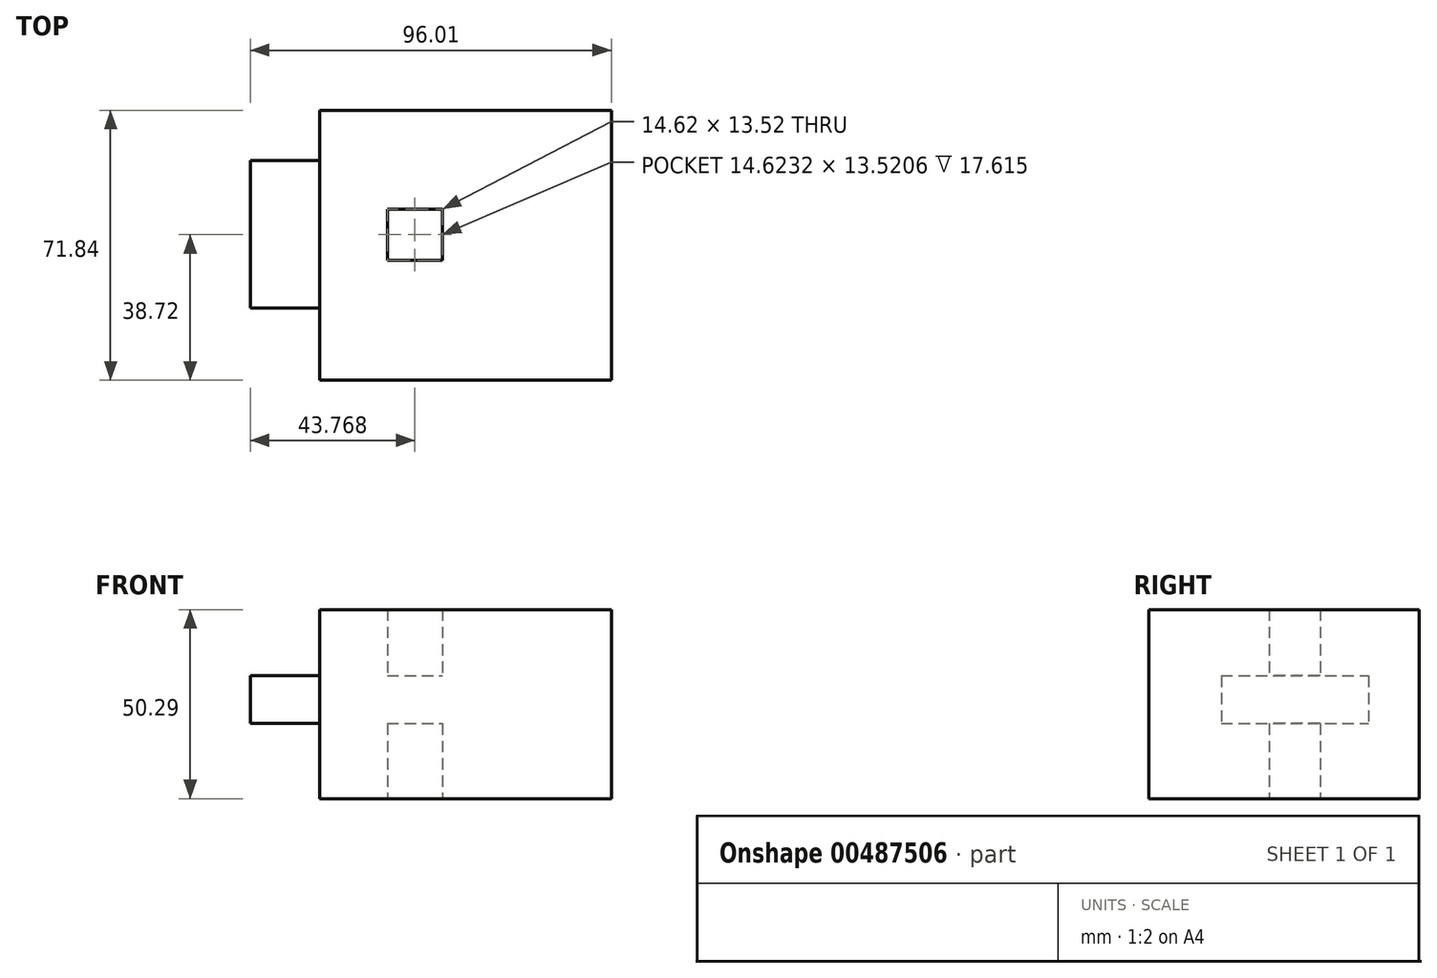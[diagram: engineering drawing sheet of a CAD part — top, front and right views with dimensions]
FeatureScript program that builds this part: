
annotation { "Feature Type Name" : "Feature", "Feature Type Description" : "" }
export const myFeature = defineFeature(function(context is Context, id is Id, definition is map)
    precondition{}
    {
        {
            var Q0;
            Q0=qCreatedBy(makeId("Top.planeOp"),FACE);
            var sketch = newSketch(context, id + "F0", { "sketchPlane" : qUnion([Q0])});
            skLineSegment(sketch, "E0.bottom", {"start": v(-32.68, 39.88) * mm, "end": v(44.93, 39.88) * mm});
            skLineSegment(sketch, "E0.top", {"start": v(-32.68, -31.96) * mm, "end": v(44.93, -31.96) * mm});
            skLineSegment(sketch, "E0.left", {"start": v(-32.68, 39.88) * mm, "end": v(-32.68, -31.96) * mm});
            skLineSegment(sketch, "E0.right", {"start": v(44.93, 39.88) * mm, "end": v(44.93, -31.96) * mm});
            skLineSegment(sketch, "E1.bottom", {"start": v(0, 0) * mm, "end": v(-14.62, 0) * mm});
            skLineSegment(sketch, "E1.top", {"start": v(0, 13.52) * mm, "end": v(-14.62, 13.52) * mm});
            skLineSegment(sketch, "E1.left", {"start": v(0, 0) * mm, "end": v(0, 13.52) * mm});
            skLineSegment(sketch, "E1.right", {"start": v(-14.62, 0) * mm, "end": v(-14.62, 13.52) * mm});
            skSolve(sketch);
        }
        {
            var Q0;
            Q0 = qSketchRegion(id + "F0", true);
            extrude(context, id + "F1", {"entities" : qUnion([Q0]), "depth" : 50.3 * mm});
        }
        {
            var Q0;
            Q0=makeQuery(id+"F1.opExtrude","SWEPT_FACE",FACE,{"disambiguationData":[OSD([sQuery(id+"F0.wireOp",EDGE,"E0.right")])]});
            var sketch = newSketch(context, id + "F2", { "sketchPlane" : qUnion([Q0])});
            skLineSegment(sketch, "E2.bottom", {"start": v(-12.73, 32.68) * mm, "end": v(26.43, 32.68) * mm});
            skLineSegment(sketch, "E2.top", {"start": v(-12.73, 19.94) * mm, "end": v(26.43, 19.94) * mm});
            skLineSegment(sketch, "E2.left", {"start": v(-12.73, 32.68) * mm, "end": v(-12.73, 19.94) * mm});
            skLineSegment(sketch, "E2.right", {"start": v(26.43, 32.68) * mm, "end": v(26.43, 19.94) * mm});
            skSolve(sketch);
        }
        {
            var Q0;
            Q0=makeQuery(id+"F2.imprint","IMPRINT",FACE,{"disambiguationData":[TD([[makeQuery(id+"F2.imprint","IMPRINT",EDGE,{"derivedFrom":sQuery(id+"F2.wireOp",EDGE,"E2.bottom")}),-1.0]])]});
            extrude(context, id + "F3", {"entities" : qUnion([Q0]), "operationType" : NewBodyOperationType.ADD, "oppositeDirection" : true, "depth" : 96.01 * mm});
        }
    });
